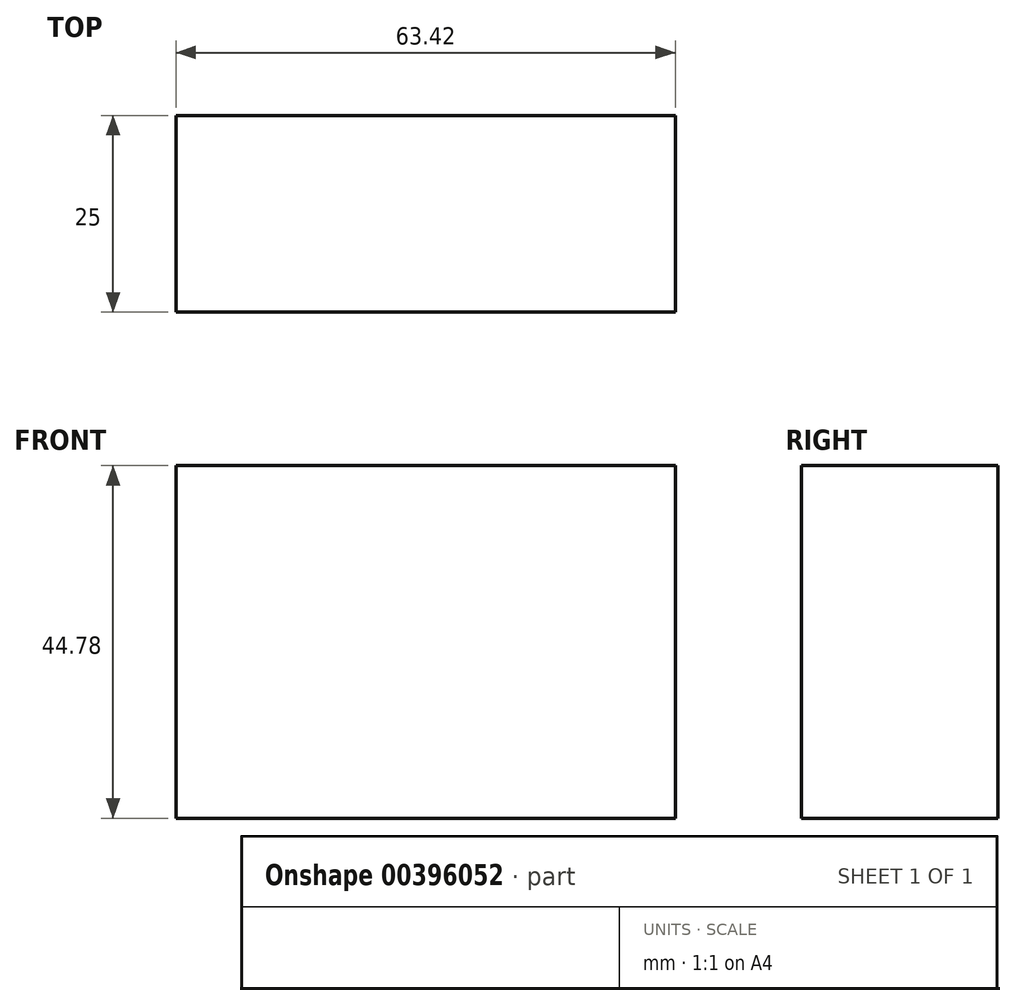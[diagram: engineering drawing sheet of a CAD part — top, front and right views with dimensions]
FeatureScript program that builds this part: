
annotation { "Feature Type Name" : "Feature", "Feature Type Description" : "" }
export const myFeature = defineFeature(function(context is Context, id is Id, definition is map)
    precondition{}
    {
        {
            var Q0;
            Q0=qCreatedBy(makeId("Front.planeOp"),FACE);
            var sketch = newSketch(context, id + "F0", { "sketchPlane" : qUnion([Q0])});
            skLineSegment(sketch, "E0.bottom", {"start": v(0, 0) * mm, "end": v(-63.42, 0) * mm});
            skLineSegment(sketch, "E0.top", {"start": v(0, 44.78) * mm, "end": v(-63.42, 44.78) * mm});
            skLineSegment(sketch, "E0.left", {"start": v(0, 0) * mm, "end": v(0, 44.78) * mm});
            skLineSegment(sketch, "E0.right", {"start": v(-63.42, 0) * mm, "end": v(-63.42, 44.78) * mm});
            skSolve(sketch);
        }
        {
            var Q0;
            Q0=makeQuery(id+"F0.imprint","IMPRINT",FACE,{"disambiguationData":[TD([[makeQuery(id+"F0.imprint","IMPRINT",EDGE,{"derivedFrom":sQuery(id+"F0.wireOp",EDGE,"E0.bottom")}),-1.0]])]});
            extrude(context, id + "F1", {"entities" : qUnion([Q0]), "depth" : 25 * mm});
        }
    });
